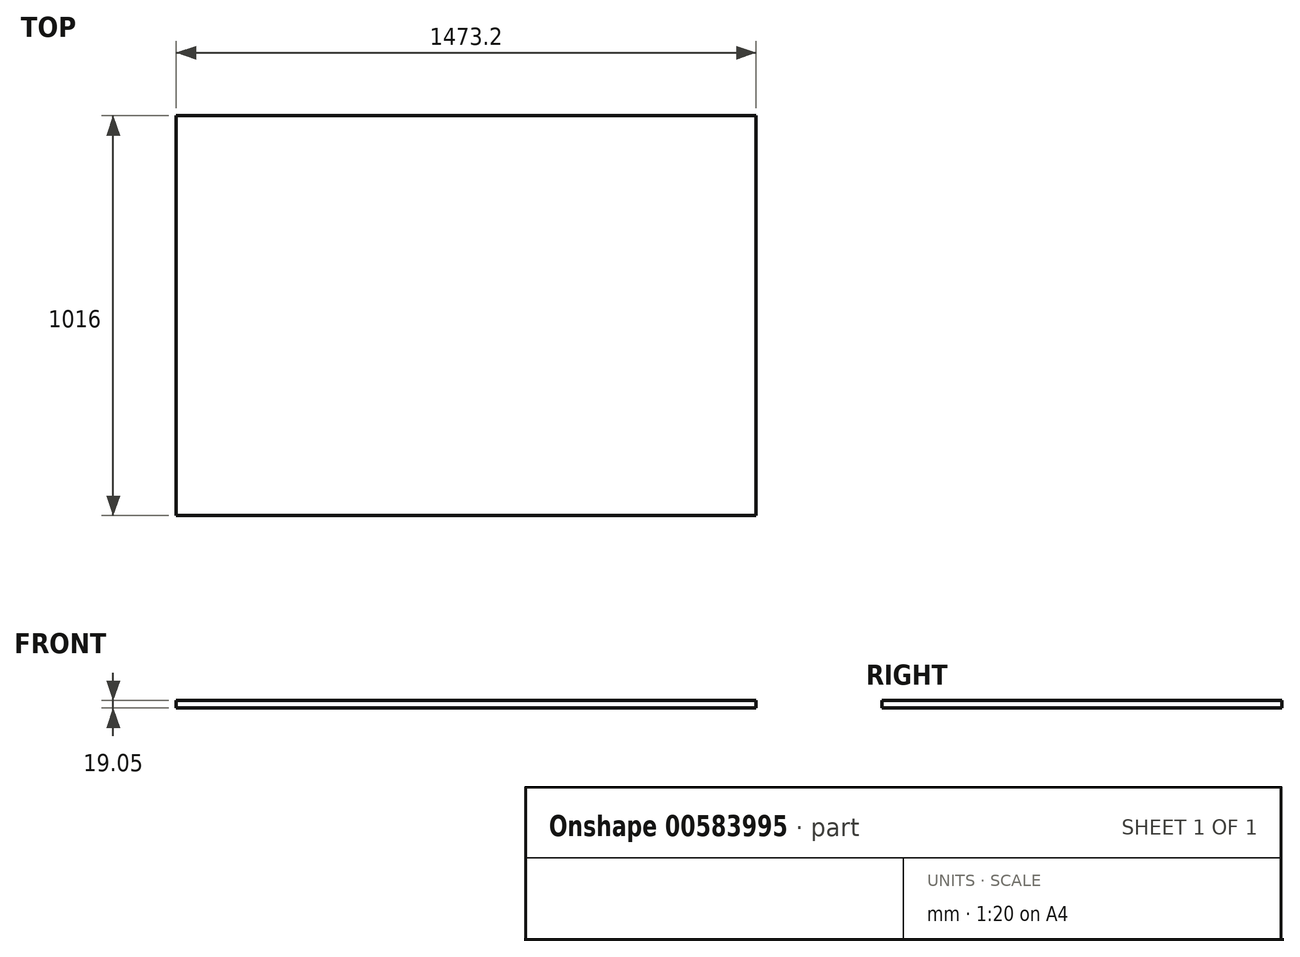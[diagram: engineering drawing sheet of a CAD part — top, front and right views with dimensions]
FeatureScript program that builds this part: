
annotation { "Feature Type Name" : "Feature", "Feature Type Description" : "" }
export const myFeature = defineFeature(function(context is Context, id is Id, definition is map)
    precondition{}
    {
        {
            var Q0;
            Q0=qCreatedBy(makeId("Top.planeOp"),FACE);
            var sketch = newSketch(context, id + "F0", { "sketchPlane" : qUnion([Q0])});
            skLineSegment(sketch, "E0.bottom", {"start": v(-725.08, 650.46) * mm, "end": v(748.12, 650.46) * mm});
            skLineSegment(sketch, "E0.top", {"start": v(-725.08, -365.54) * mm, "end": v(748.12, -365.54) * mm});
            skLineSegment(sketch, "E0.left", {"start": v(-725.08, 650.46) * mm, "end": v(-725.08, -365.54) * mm});
            skLineSegment(sketch, "E0.right", {"start": v(748.12, 650.46) * mm, "end": v(748.12, -365.54) * mm});
            skSolve(sketch);
        }
        {
            var Q0;
            Q0=makeQuery(id+"F0.imprint","IMPRINT",FACE,{"disambiguationData":[TD([[makeQuery(id+"F0.imprint","IMPRINT",EDGE,{"derivedFrom":sQuery(id+"F0.wireOp",EDGE,"E0.bottom")}),-1.0]])]});
            extrude(context, id + "F1", {"entities" : qUnion([Q0]), "depth" : 19.05 * mm, "offsetDistance" : 25.4 * mm});
        }
    });
